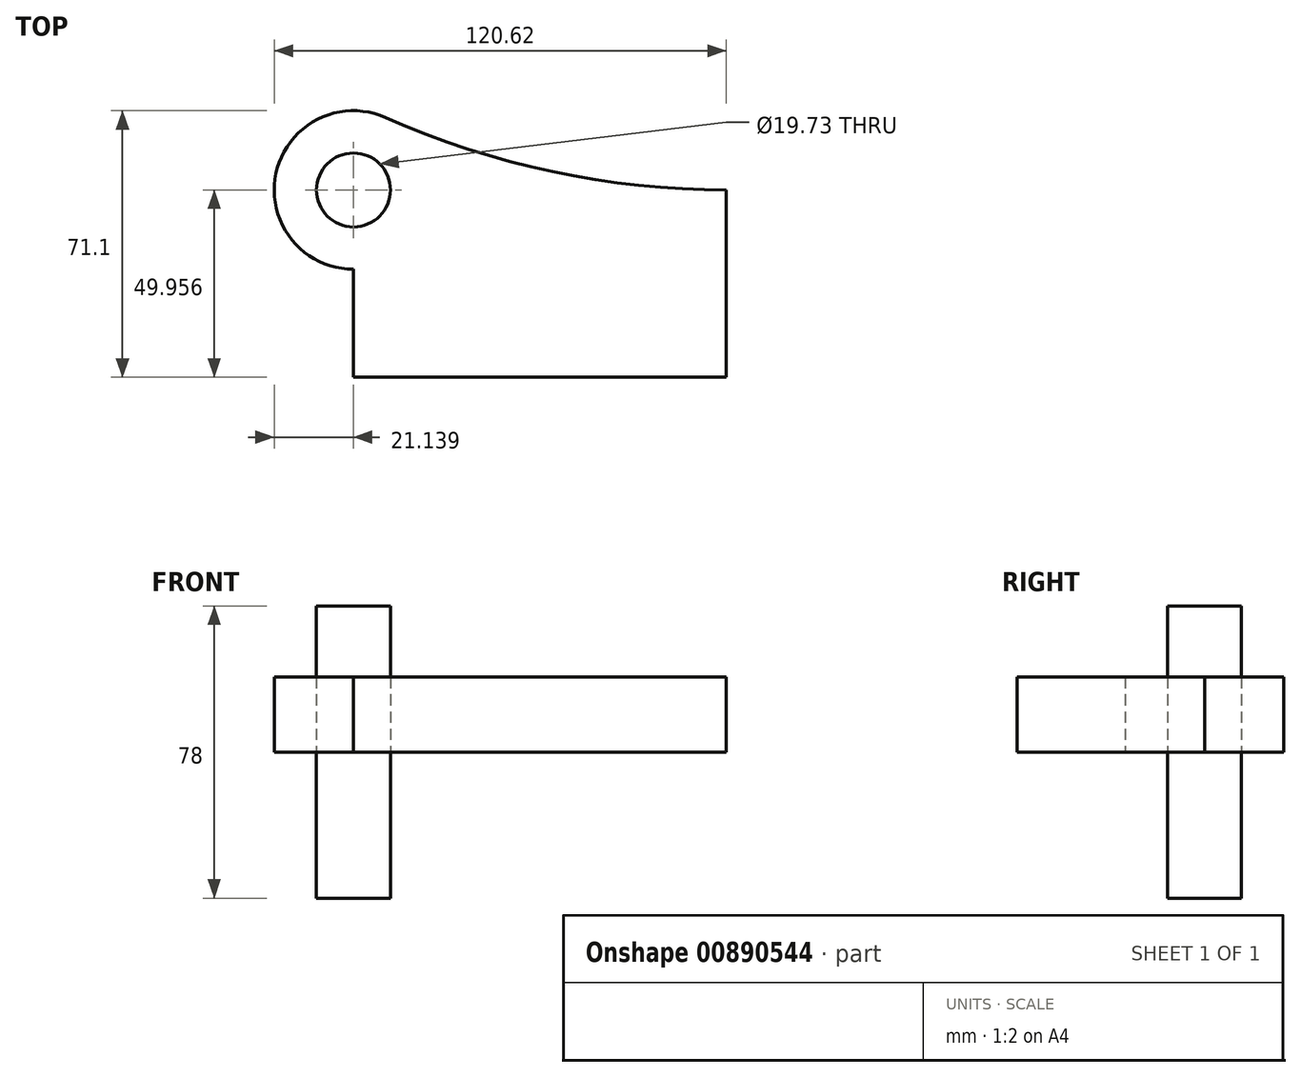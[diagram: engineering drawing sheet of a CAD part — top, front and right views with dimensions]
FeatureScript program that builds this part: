
annotation { "Feature Type Name" : "Feature", "Feature Type Description" : "" }
export const myFeature = defineFeature(function(context is Context, id is Id, definition is map)
    precondition{}
    {
        {
            var Q0;
            Q0=qCreatedBy(makeId("Top.planeOp"),FACE);
            var sketch = newSketch(context, id + "F0", { "sketchPlane" : qUnion([Q0])});
            skLineSegment(sketch, "E0.bottom", {"start": v(49.74, -24.98) * mm, "end": v(-49.74, -24.98) * mm});
            skLineSegment(sketch, "E0.top", {"start": v(49.74, 24.98) * mm, "end": v(-49.74, 24.98) * mm});
            skLineSegment(sketch, "E0.left", {"start": v(49.74, -24.98) * mm, "end": v(49.74, 24.98) * mm});
            skLineSegment(sketch, "E0.right", {"start": v(-49.74, -24.98) * mm, "end": v(-49.74, 24.98) * mm});
            skPoint(sketch, "E0.middle", {"position": v(0, 0) * mm});
            skCircle(sketch, "E1", {"center": v(-49.74, 24.98) * mm, "radius": 21.14 * mm});
            skArc(sketch, "E2", {"start": v(-41.14, 44.3) * mm, "mid": v(3.28, 29.86) * mm, "end": v(49.74, 24.98) * mm});
            skCircle(sketch, "E3", {"center": v(-49.74, 24.98) * mm, "radius": 9.87 * mm});
            skSolve(sketch);
        }
        {
            var Q0;
            Q0 = qSketchRegion(id + "F0", true);
            extrude(context, id + "F1", {"entities" : qUnion([Q0]), "depth" : 20 * mm, "offsetDistance" : 25 * mm});
        }
        {
            var Q0;
            {var subQ0=sQuery(id+"F0.wireOp",EDGE,"E0.right");var subQ1=sQuery(id+"F0.wireOp",EDGE,"E0.top");var subQ2=makeQuery(id+"F0.imprint","INTERSECT",VERTEX,{"derivedFrom":[subQ1,subQ0]});Q0=makeQuery(id+"F0.imprint","IMPRINT",FACE,{"disambiguationData":[TD([[makeQuery(id+"F0.imprint","IMPRINT",EDGE,{"disambiguationData":[TD([[subQ2,1.0]])],"derivedFrom":subQ1}),-1.0]])]});}
            var Q1;
            {var subQ0=sQuery(id+"F0.wireOp",EDGE,"E0.right");var subQ1=sQuery(id+"F0.wireOp",EDGE,"E0.top");var subQ2=makeQuery(id+"F0.imprint","INTERSECT",VERTEX,{"derivedFrom":[subQ1,subQ0]});Q1=makeQuery(id+"F0.imprint","IMPRINT",FACE,{"disambiguationData":[TD([[makeQuery(id+"F0.imprint","IMPRINT",EDGE,{"disambiguationData":[TD([[subQ2,1.0]])],"derivedFrom":subQ1}),1.0]])]});}
            extrude(context, id + "F2", {"entities" : qUnion([Q0, Q1]), "endBound" : BoundingType.SYMMETRIC, "depth" : 78 * mm, "offsetDistance" : 25 * mm});
        }
    });
